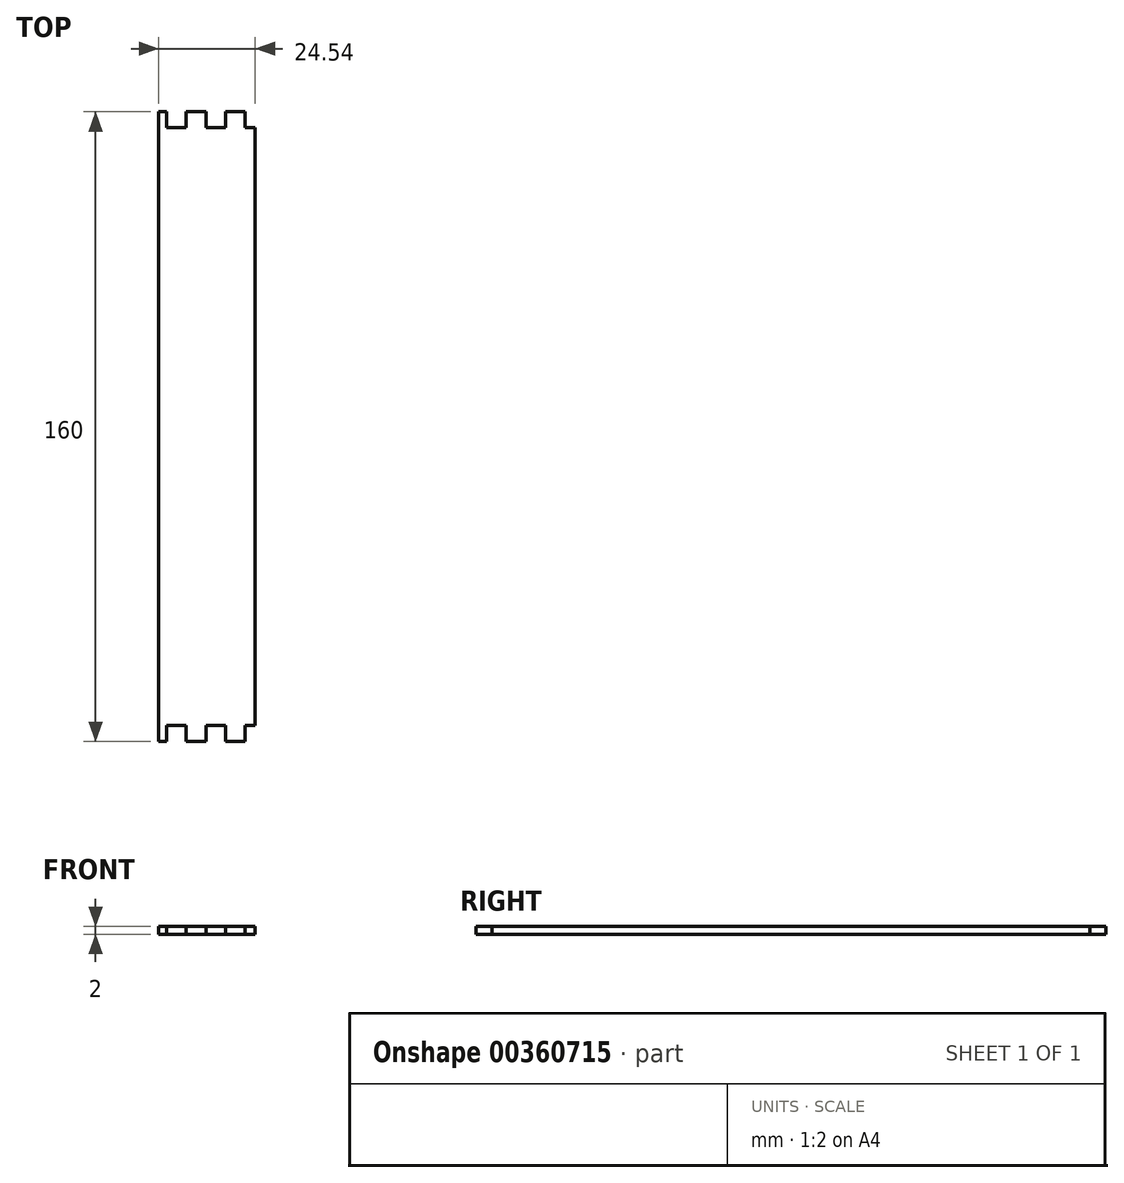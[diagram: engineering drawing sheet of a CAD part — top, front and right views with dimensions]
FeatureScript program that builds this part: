
annotation { "Feature Type Name" : "Feature", "Feature Type Description" : "" }
export const myFeature = defineFeature(function(context is Context, id is Id, definition is map)
    precondition{}
    {
        {
            var Q0;
            Q0=qCreatedBy(makeId("Top.planeOp"),FACE);
            var sketch = newSketch(context, id + "F0", { "sketchPlane" : qUnion([Q0])});
            skLineSegment(sketch, "E0", {"start": v(0, 115.27) * mm, "end": v(0, -113.6) * mm, "construction": true});
            skLineSegment(sketch, "E1", {"start": v(106.07, 0) * mm, "end": v(-105.69, 0) * mm, "construction": true});
            skLineSegment(sketch, "E2", {"start": v(0, -80) * mm, "end": v(24.54, -80) * mm});
            skLineSegment(sketch, "E3", {"start": v(24.54, -80) * mm, "end": v(24.54, 0) * mm});
            skLineSegment(sketch, "E4.MirrorCS", {"start": v(24.54, 80) * mm, "end": v(24.54, 0) * mm});
            skLineSegment(sketch, "E5.MirrorCS", {"start": v(0, 80) * mm, "end": v(24.54, 80) * mm});
            skLineSegment(sketch, "E6.MirrorCS", {"start": v(0, 80) * mm, "end": v(-24.54, 80) * mm});
            skLineSegment(sketch, "E7.MirrorCS", {"start": v(-24.54, 80) * mm, "end": v(-24.54, 0) * mm});
            skLineSegment(sketch, "E8.MirrorCS", {"start": v(-24.54, -80) * mm, "end": v(-24.54, 0) * mm});
            skLineSegment(sketch, "E9.MirrorCS", {"start": v(0, -80) * mm, "end": v(-24.54, -80) * mm});
            skSolve(sketch);
        }
        {
            var Q0;
            Q0 = qSketchRegion(id + "F0", true);
            extrude(context, id + "F1", {"entities" : qUnion([Q0]), "depth" : 2 * mm});
        }
        {
            var Q0;
            Q0=makeQuery(id+"F1.opExtrude","CAP_FACE",FACE,{"disambiguationData":[OSD([sQuery(id+"F0.wireOp",EDGE,"E2"),sQuery(id+"F0.wireOp",EDGE,"E3"),sQuery(id+"F0.wireOp",EDGE,"E4.MirrorCS"),sQuery(id+"F0.wireOp",EDGE,"E5.MirrorCS"),sQuery(id+"F0.wireOp",EDGE,"E6.MirrorCS"),sQuery(id+"F0.wireOp",EDGE,"E7.MirrorCS"),sQuery(id+"F0.wireOp",EDGE,"E8.MirrorCS"),sQuery(id+"F0.wireOp",EDGE,"E9.MirrorCS")])],"isStart":false});
            var sketch = newSketch(context, id + "F2", { "sketchPlane" : qUnion([Q0])});
            skLineSegment(sketch, "E10", {"start": v(-94.86, 0) * mm, "end": v(69.14, 0) * mm, "construction": true});
            skLineSegment(sketch, "E11", {"start": v(0, -57) * mm, "end": v(0, -88.63) * mm, "construction": true});
            skLineSegment(sketch, "E12", {"start": v(0, -76) * mm, "end": v(2.5, -76) * mm});
            skLineSegment(sketch, "E13", {"start": v(2.5, -76) * mm, "end": v(2.5, -80) * mm});
            skLineSegment(sketch, "E14", {"start": v(2.5, -80) * mm, "end": v(7.5, -80) * mm});
            skLineSegment(sketch, "E15", {"start": v(7.5, -80) * mm, "end": v(7.5, -76) * mm});
            skLineSegment(sketch, "E16", {"start": v(7.5, -76) * mm, "end": v(12.5, -76) * mm});
            skLineSegment(sketch, "E17", {"start": v(12.5, -76) * mm, "end": v(12.5, -80) * mm});
            skLineSegment(sketch, "E18", {"start": v(12.5, -80) * mm, "end": v(17.5, -80) * mm});
            skLineSegment(sketch, "E19", {"start": v(17.5, -80) * mm, "end": v(17.5, -76) * mm});
            skLineSegment(sketch, "E20", {"start": v(17.5, -76) * mm, "end": v(22.5, -76) * mm});
            skLineSegment(sketch, "E21", {"start": v(22.5, -76) * mm, "end": v(22.5, -80) * mm});
            skLineSegment(sketch, "E22.MirrorCS", {"start": v(0, -76) * mm, "end": v(-2.5, -76) * mm});
            skLineSegment(sketch, "E23.MirrorCS", {"start": v(-2.5, -76) * mm, "end": v(-2.5, -80) * mm});
            skLineSegment(sketch, "E24.MirrorCS", {"start": v(-2.5, -80) * mm, "end": v(-7.5, -80) * mm});
            skLineSegment(sketch, "E25.MirrorCS", {"start": v(-7.5, -80) * mm, "end": v(-7.5, -76) * mm});
            skLineSegment(sketch, "E26.MirrorCS", {"start": v(-7.5, -76) * mm, "end": v(-12.5, -76) * mm});
            skLineSegment(sketch, "E27.MirrorCS", {"start": v(-17.5, -76) * mm, "end": v(-22.5, -76) * mm});
            skLineSegment(sketch, "E28.MirrorCS", {"start": v(-17.5, -80) * mm, "end": v(-17.5, -76) * mm});
            skLineSegment(sketch, "E29.MirrorCS", {"start": v(-22.5, -76) * mm, "end": v(-22.5, -80) * mm});
            skLineSegment(sketch, "E30.MirrorCS", {"start": v(-12.5, -80) * mm, "end": v(-17.5, -80) * mm});
            skLineSegment(sketch, "E31.MirrorCS", {"start": v(-12.5, -76) * mm, "end": v(-12.5, -80) * mm});
            skLineSegment(sketch, "E32", {"start": v(-22.5, -80) * mm, "end": v(-22.5, -83.7) * mm});
            skLineSegment(sketch, "E33", {"start": v(-22.5, -83.7) * mm, "end": v(22.5, -83.7) * mm});
            skLineSegment(sketch, "E34", {"start": v(22.5, -83.7) * mm, "end": v(22.5, -80) * mm});
            skLineSegment(sketch, "E35.MirrorCS", {"start": v(-22.5, 76) * mm, "end": v(-22.5, 80) * mm});
            skLineSegment(sketch, "E36.MirrorCS", {"start": v(-17.5, 76) * mm, "end": v(-22.5, 76) * mm});
            skLineSegment(sketch, "E37.MirrorCS", {"start": v(-17.5, 80) * mm, "end": v(-17.5, 76) * mm});
            skLineSegment(sketch, "E38.MirrorCS", {"start": v(-12.5, 80) * mm, "end": v(-17.5, 80) * mm});
            skLineSegment(sketch, "E39.MirrorCS", {"start": v(-7.5, 76) * mm, "end": v(-12.5, 76) * mm});
            skLineSegment(sketch, "E40.MirrorCS", {"start": v(-7.5, 80) * mm, "end": v(-7.5, 76) * mm});
            skLineSegment(sketch, "E41.MirrorCS", {"start": v(-2.5, 76) * mm, "end": v(-2.5, 80) * mm});
            skLineSegment(sketch, "E42.MirrorCS", {"start": v(0, 76) * mm, "end": v(-2.5, 76) * mm});
            skLineSegment(sketch, "E43.MirrorCS", {"start": v(0, 76) * mm, "end": v(2.5, 76) * mm});
            skLineSegment(sketch, "E44.MirrorCS", {"start": v(2.5, 76) * mm, "end": v(2.5, 80) * mm});
            skLineSegment(sketch, "E45.MirrorCS", {"start": v(2.5, 80) * mm, "end": v(7.5, 80) * mm});
            skLineSegment(sketch, "E46.MirrorCS", {"start": v(7.5, 80) * mm, "end": v(7.5, 76) * mm});
            skLineSegment(sketch, "E47.MirrorCS", {"start": v(7.5, 76) * mm, "end": v(12.5, 76) * mm});
            skLineSegment(sketch, "E48.MirrorCS", {"start": v(12.5, 80) * mm, "end": v(17.5, 80) * mm});
            skLineSegment(sketch, "E49.MirrorCS", {"start": v(17.5, 80) * mm, "end": v(17.5, 76) * mm});
            skLineSegment(sketch, "E50.MirrorCS", {"start": v(17.5, 76) * mm, "end": v(22.5, 76) * mm});
            skLineSegment(sketch, "E51.MirrorCS", {"start": v(22.5, 83.7) * mm, "end": v(22.5, 80) * mm});
            skLineSegment(sketch, "E52.MirrorCS", {"start": v(-22.5, 83.7) * mm, "end": v(22.5, 83.7) * mm});
            skLineSegment(sketch, "E53.MirrorCS", {"start": v(-12.5, 76) * mm, "end": v(-12.5, 80) * mm});
            skLineSegment(sketch, "E54.MirrorCS", {"start": v(-2.5, 80) * mm, "end": v(-7.5, 80) * mm});
            skLineSegment(sketch, "E55.MirrorCS", {"start": v(-22.5, 80) * mm, "end": v(-22.5, 83.7) * mm});
            skLineSegment(sketch, "E56.MirrorCS", {"start": v(22.5, 76) * mm, "end": v(22.5, 80) * mm});
            skLineSegment(sketch, "E57.MirrorCS", {"start": v(12.5, 76) * mm, "end": v(12.5, 80) * mm});
            skSolve(sketch);
        }
        {
            var Q0;
            Q0 = qSketchRegion(id + "F2", true);
            extrude(context, id + "F3", {"entities" : qUnion([Q0]), "operationType" : NewBodyOperationType.REMOVE, "oppositeDirection" : true, "depth" : 5 * mm});
        }
        {
            var Q0;
            Q0=makeQuery(id+"F1.opExtrude","CAP_FACE",FACE,{"disambiguationData":[OSD([sQuery(id+"F0.wireOp",EDGE,"E2"),sQuery(id+"F0.wireOp",EDGE,"E3"),sQuery(id+"F0.wireOp",EDGE,"E4.MirrorCS"),sQuery(id+"F0.wireOp",EDGE,"E5.MirrorCS"),sQuery(id+"F0.wireOp",EDGE,"E6.MirrorCS"),sQuery(id+"F0.wireOp",EDGE,"E7.MirrorCS"),sQuery(id+"F0.wireOp",EDGE,"E8.MirrorCS"),sQuery(id+"F0.wireOp",EDGE,"E9.MirrorCS")])],"isStart":false});
            var sketch = newSketch(context, id + "F4", { "sketchPlane" : qUnion([Q0])});
            skLineSegment(sketch, "E58", {"start": v(0, 110.68) * mm, "end": v(0, -94.42) * mm});
            skLineSegment(sketch, "E59", {"start": v(0, -94.42) * mm, "end": v(28.97, -94.42) * mm});
            skLineSegment(sketch, "E60", {"start": v(28.97, -94.42) * mm, "end": v(28.97, 110.68) * mm});
            skLineSegment(sketch, "E61", {"start": v(28.97, 110.68) * mm, "end": v(0, 110.68) * mm});
            skSolve(sketch);
        }
        {
            var Q0;
            Q0 = qSketchRegion(id + "F4", true);
            extrude(context, id + "F5", {"entities" : qUnion([Q0]), "operationType" : NewBodyOperationType.REMOVE, "oppositeDirection" : true, "depth" : 25 * mm});
        }
    });
